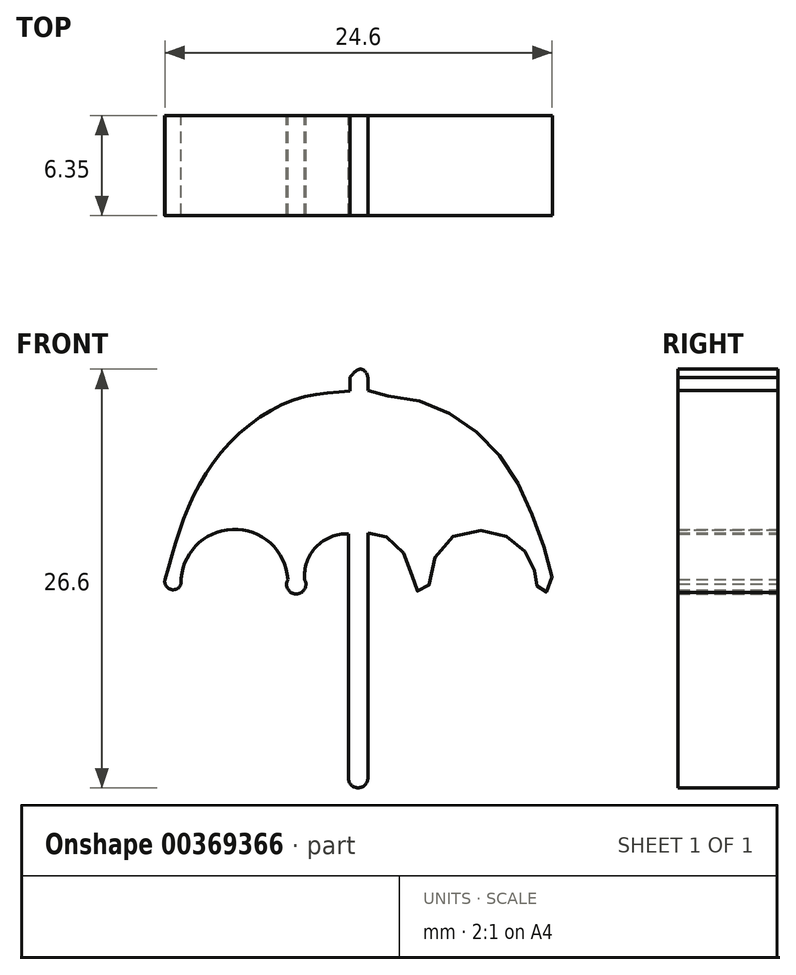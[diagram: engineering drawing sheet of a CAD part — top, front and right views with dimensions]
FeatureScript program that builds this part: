
annotation { "Feature Type Name" : "Feature", "Feature Type Description" : "" }
export const myFeature = defineFeature(function(context is Context, id is Id, definition is map)
    precondition{}
    {
        {
            var Q0;
            Q0=qCreatedBy(makeId("Front.planeOp"),FACE);
            var sketch = newSketch(context, id + "F0", { "sketchPlane" : qUnion([Q0])});
            skArc(sketch, "E0", {"start": v(-12.45, -0.65) * mm, "mid": v(-12.07, -1.28) * mm, "end": v(-11.43, -0.92) * mm});
            skFitSpline(sketch, "E1", {"points": [v(-12.45, -0.65) * mm, v(-11, 3.86) * mm, v(-8.48, 7.89) * mm, v(-4.5, 10.68) * mm, v(-0.7, 11.32) * mm], "startDerivative": vector(4.93, 17.97) * mm, "endDerivative": vector(16.51, 1.07) * mm});
            skLineSegment(sketch, "E2", {"start": v(-0.7, 11.32) * mm, "end": v(-0.7, 12.23) * mm});
            skLineSegment(sketch, "E3", {"start": v(0.43, 12.18) * mm, "end": v(0.43, 11.37) * mm});
            skFitSpline(sketch, "E4", {"points": [v(-0.7, 12.23) * mm, v(0, 12.72) * mm, v(0.43, 12.18) * mm, v(0.43, 11.37) * mm, v(2.8, 10.9) * mm, v(6.6, 9.28) * mm, v(9.55, 6.17) * mm, v(11.43, 1.93) * mm, v(12.08, -1.13) * mm, v(11.54, -1.45) * mm, v(11.16, -1.02) * mm, v(11, 0) * mm, v(9.98, 1.6) * mm, v(7.62, 2.46) * mm, v(4.94, 1.28) * mm, v(4.13, -1.35) * mm, v(3.49, -1.3) * mm, v(3.17, 0) * mm, v(1.83, 1.93) * mm, v(0.43, 2.3) * mm], "startDerivative": vector(19.81, 21.31) * mm, "endDerivative": vector(-30.25, 2.36) * mm});
            skLineSegment(sketch, "E5", {"start": v(0.9, 2.27) * mm, "end": v(0.43, 2.3) * mm});
            skLineSegment(sketch, "E6", {"start": v(0.43, 2.3) * mm, "end": v(0.43, -13.26) * mm});
            skArc(sketch, "E7", {"start": v(-0.8, -13.26) * mm, "mid": v(-0.19, -13.88) * mm, "end": v(0.43, -13.26) * mm});
            skLineSegment(sketch, "E8", {"start": v(-0.8, -13.26) * mm, "end": v(-0.8, 2.25) * mm});
            skArc(sketch, "E9", {"start": v(-4.65, -0.65) * mm, "mid": v(-8.17, 2.54) * mm, "end": v(-11.43, -0.92) * mm});
            skArc(sketch, "E10", {"start": v(-0.8, 2.25) * mm, "mid": v(-2.85, 1.43) * mm, "end": v(-3.58, -0.65) * mm});
            skArc(sketch, "E11", {"start": v(-4.65, -0.65) * mm, "mid": v(-4.12, -1.56) * mm, "end": v(-3.58, -0.65) * mm});
            skArc(sketch, "E12", {"start": v(-4.65, 2.25) * mm, "mid": v(-7.51, 3.5) * mm, "end": v(-10.54, 2.75) * mm});
            skArc(sketch, "E13", {"start": v(3.39, 1.93) * mm, "mid": v(-0.15, 3.37) * mm, "end": v(-3.7, 1.93) * mm});
            skArc(sketch, "E14", {"start": v(10.07, 2.75) * mm, "mid": v(7.27, 3.44) * mm, "end": v(4.64, 2.25) * mm});
            skFitSpline(sketch, "E15", {"points": [v(-2.44, 10.22) * mm, v(-4.2, 9.83) * mm, v(-6.58, 8.58) * mm, v(-8.56, 6.49) * mm, v(-10.54, 2.75) * mm], "startDerivative": vector(-8.48, -1.38) * mm, "endDerivative": vector(-6.26, -13.2) * mm});
            skFitSpline(sketch, "E16", {"points": [v(-4.65, 2.25) * mm, v(-4.65, 4.67) * mm, v(-4.26, 6.83) * mm, v(-3.7, 8.58) * mm, v(-3, 9.43) * mm, v(-2.44, 10.22) * mm], "startDerivative": vector(-0.44, 10.17) * mm, "endDerivative": vector(3.45, 5.32) * mm});
            skFitSpline(sketch, "E17", {"points": [v(-0.14, 10.46) * mm, v(-1.13, 10) * mm, v(-2.01, 9.23) * mm, v(-2.7, 8.3) * mm, v(-3.2, 7.08) * mm, v(-3.6, 5.78) * mm, v(-3.76, 2.83) * mm, v(-3.7, 1.93) * mm], "startDerivative": vector(-8.02, -3) * mm, "endDerivative": vector(0.78, -6.22) * mm});
            skFitSpline(sketch, "E18", {"points": [v(-0.14, 10.46) * mm, v(0.65, 10.22) * mm, v(1.44, 9.6) * mm, v(1.95, 9.2) * mm, v(2.75, 7.9) * mm, v(3.17, 6.85) * mm, v(3.4, 5.52) * mm, v(3.51, 3.28) * mm, v(3.39, 1.93) * mm], "startDerivative": vector(7.77, -1.3) * mm, "endDerivative": vector(-1.24, -9.38) * mm});
            skFitSpline(sketch, "E19", {"points": [v(4.64, 2.25) * mm, v(4.64, 4.41) * mm, v(4.13, 6.93) * mm, v(3.39, 8.89) * mm, v(2.12, 10.22) * mm], "startDerivative": vector(0.44, 8.44) * mm, "endDerivative": vector(-6.08, 5.32) * mm});
            skFitSpline(sketch, "E20", {"points": [v(2.12, 10.22) * mm, v(3.17, 10.22) * mm, v(5.52, 9.06) * mm, v(6.85, 8.1) * mm, v(8.5, 6.17) * mm, v(9.65, 4.07) * mm, v(10.07, 2.75) * mm], "startDerivative": vector(7.45, 1.3) * mm, "endDerivative": vector(2.31, -8.83) * mm});
            skSolve(sketch);
        }
        {
            var Q0;
            Q0=makeQuery(id+"F0.imprint","IMPRINT",FACE,{"disambiguationData":[TD([[makeQuery(id+"F0.imprint","IMPRINT",EDGE,{"derivedFrom":sQuery(id+"F0.wireOp",EDGE,"E13")}),-1.0]])]});
            var Q1;
            Q1=makeQuery(id+"F0.imprint","IMPRINT",FACE,{"disambiguationData":[TD([[makeQuery(id+"F0.imprint","IMPRINT",EDGE,{"derivedFrom":sQuery(id+"F0.wireOp",EDGE,"E14")}),-1.0]])]});
            var Q2;
            {var subQ0=sQuery(id+"F0.wireOp",EDGE,"E4");var subQ1=sQuery(id+"F0.wireOp",EDGE,"E3");var subQ2=makeQuery(id+"F0.imprint","INTERSECT",VERTEX,{"disambiguationData":[OD(1.0)],"derivedFrom":[subQ1,subQ0]});Q2=makeQuery(id+"F0.imprint","IMPRINT",FACE,{"disambiguationData":[TD([[makeQuery(id+"F0.imprint","IMPRINT",EDGE,{"disambiguationData":[TD([[subQ2,1.0]])],"derivedFrom":subQ1}),-1.0]])]});}
            var Q3;
            {var subQ0=sQuery(id+"F0.wireOp",EDGE,"E4");var subQ1=sQuery(id+"F0.wireOp",EDGE,"E3");var subQ2=makeQuery(id+"F0.imprint","INTERSECT",VERTEX,{"disambiguationData":[OD(0.0)],"derivedFrom":[subQ1,subQ0]});Q3=makeQuery(id+"F0.imprint","IMPRINT",FACE,{"disambiguationData":[TD([[makeQuery(id+"F0.imprint","IMPRINT",EDGE,{"disambiguationData":[TD([[subQ2,-1.0]])],"derivedFrom":subQ1}),1.0]])]});}
            var Q4;
            Q4=makeQuery(id+"F0.imprint","IMPRINT",FACE,{"disambiguationData":[TD([[makeQuery(id+"F0.imprint","IMPRINT",EDGE,{"derivedFrom":sQuery(id+"F0.wireOp",EDGE,"E12")}),-1.0]])]});
            var Q5;
            Q5=makeQuery(id+"F0.imprint","IMPRINT",FACE,{"disambiguationData":[TD([[makeQuery(id+"F0.imprint","IMPRINT",EDGE,{"derivedFrom":sQuery(id+"F0.wireOp",EDGE,"E0")}),1.0]])]});
            extrude(context, id + "F1", {"entities" : qUnion([Q0, Q1, Q2, Q3, Q4, Q5]), "depth" : 6.35 * mm, "offsetDistance" : 25.4 * mm});
        }
    });
